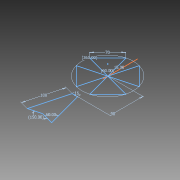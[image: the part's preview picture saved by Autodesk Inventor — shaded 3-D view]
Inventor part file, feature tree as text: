
AUTODESK INVENTOR PART (.ipt)
format: ipt  version: 2011 SP2 (Build 150309200, 309)  size: 70,144 bytes
history: native  units: mm
features: sketch x1
ambient origin geometry x8: Origin, YZ Plane, XZ Plane, XY Plane, X Axis, Y Axis, Z Axis, Center Point
feature tree (1):
  sketch  "Sketch1"  dims[d0=70.0mm d1=60.0deg d2=15.0deg d3=40.0mm d5=360.0deg d7=15.0mm d8=90.0mm d9=100.0mm d11=150.0deg d12=60.0deg]
